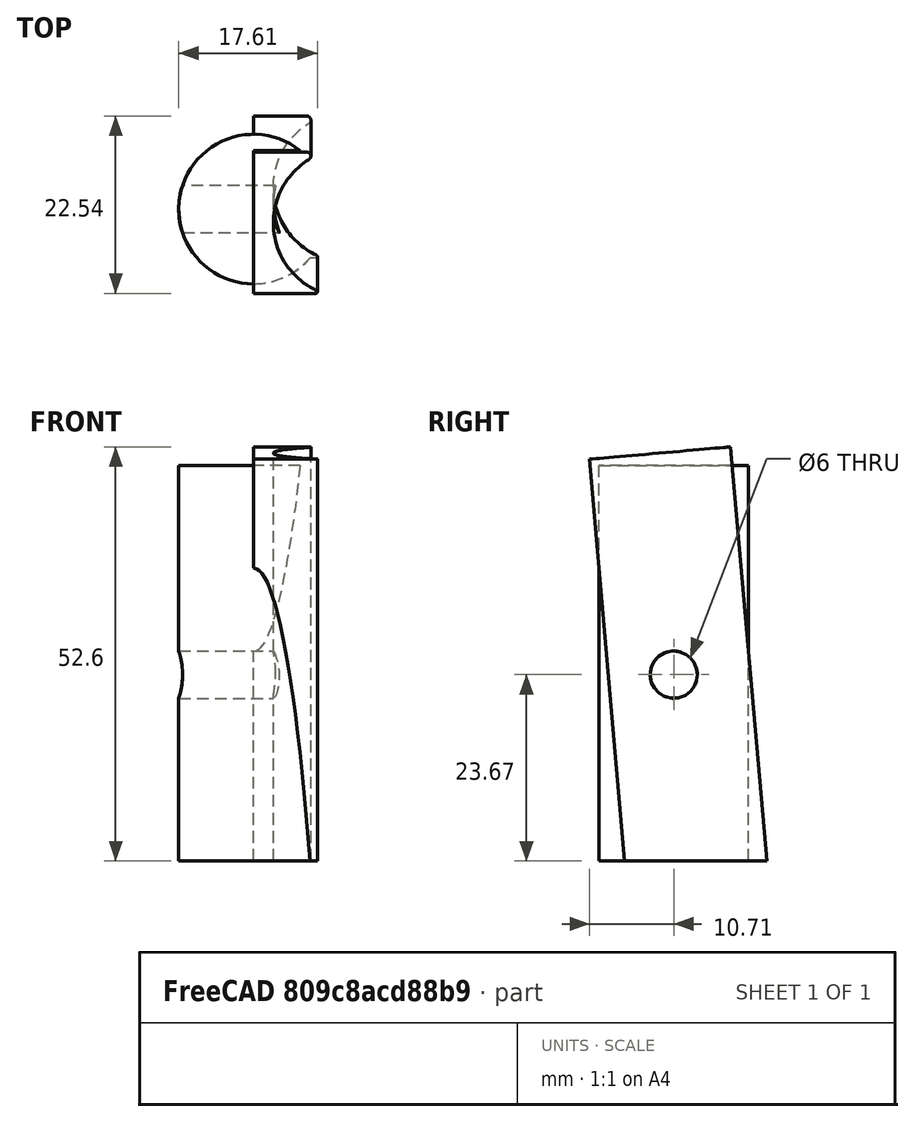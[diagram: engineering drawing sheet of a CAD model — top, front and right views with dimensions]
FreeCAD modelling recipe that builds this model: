
FCSTD DOCUMENT  (FreeCAD 0.19R)
Label: Mowerhandle.stl
License: All rights reserved
LicenseURL: http://en.wikipedia.org/wiki/All_rights_reserved
objects: Sketcher::SketchObject×3, PartDesign::Pocket×3, Mesh::Feature×2, PartDesign::Fillet×2, Part::Cylinder×1, Part::Box×1, Part::MultiFuse×1, PartDesign::FeatureBase×1, PartDesign::Body×1
note: 18 computed .brp shape members not serialized (recipe doc carries the construction recipe); baked Part::Feature solids carry a one-line shape summary decoded from their .brp

FEATURE [Mesh::Feature] MowerHandel
FEATURE [Part::Cylinder] Cylinder
  Angle = 360
  AttacherType = Attacher::AttachEngine3D
  Height = 53
  Radius = 9.5
FEATURE [Part::Box] Box  label="Cube"
  AttacherType = Attacher::AttachEngine3D
  Height = 54
  Length = 10
  Placement = pos=(0,-6,0) rot=(1,0,0;0.087266rad)
  Width = 18
FEATURE [Part::MultiFuse] Fusion
  Shapes = -> [Cylinder,Box]
FEATURE [PartDesign::FeatureBase] BaseFeature
  BaseFeature = -> Fusion
FEATURE [Sketcher::SketchObject] Sketch
  FullyConstrained = false
  MapMode = 5
  Placement = pos=(0,-4.75199,54.3155) rot=(1,0,0;0.087266rad)
  Support = -> [BaseFeature]
  sketch-geometry (1):
    g0: Circle CenterX=12.0222 CenterY=3.0075 CenterZ=0 NormalX=0 NormalY=0 NormalZ=1 AngleXU=0 Radius=9.5
  constraints (1):
    c: Radius(g0) = 9.5
FEATURE [PartDesign::Pocket] Pocket
  BaseFeature = -> BaseFeature
  Length = 5
  Length2 = 100
  Profile = -> Sketch
  Type = 1
FEATURE [PartDesign::Fillet] Fillet
  Base = -> Pocket [Edge13]
  BaseFeature = -> Pocket
  Radius = 0.5
  SupportTransform = false
FEATURE [PartDesign::Fillet] Fillet001
  Base = -> Fillet [Edge3]
  BaseFeature = -> Fillet
  Radius = 0.2
  SupportTransform = false
FEATURE [Sketcher::SketchObject] Sketch001
  FullyConstrained = false
  MapMode = 5
  Placement = pos=(0,0,0) rot=(0.57735,0.57735,0.57735;2.0944rad)
  Support = -> [YZ_Plane]
  sketch-geometry (1):
    g0: Circle CenterX=0 CenterY=26.4299 CenterZ=0 NormalX=0 NormalY=0 NormalZ=1 AngleXU=0 Radius=3
  constraints (2):
    c: PointOnObject(g0,g-2)
    c: Diameter(g0) = 6
FEATURE [PartDesign::Pocket] Pocket001
  BaseFeature = -> Fillet001
  Length = 5
  Length2 = 100
  Midplane = true
  Profile = -> Sketch001
  Type = 1
FEATURE [Sketcher::SketchObject] Sketch002
  FullyConstrained = false
  MapMode = 5
  Placement = pos=(0,0,0) rot=(0.57735,0.57735,0.57735;2.0944rad)
  Support = -> [YZ_Plane]
  sketch-geometry (4):
    g0: LineSegment StartX=-12.9286 StartY=2.76123 StartZ=0 EndX=17.649 EndY=2.76123 EndZ=0
    g1: LineSegment StartX=17.649 StartY=2.76123 StartZ=0 EndX=17.649 EndY=-9.03295 EndZ=0
    g2: LineSegment StartX=17.649 StartY=-9.03295 StartZ=0 EndX=-12.9286 EndY=-9.03295 EndZ=0
    g3: LineSegment StartX=-12.9286 StartY=-9.03295 StartZ=0 EndX=-12.9286 EndY=2.76123 EndZ=0
  constraints (8):
    c: Coincident(g0,g1)
    c: Coincident(g1,g2)
    c: Coincident(g2,g3)
    c: Coincident(g3,g0)
    c: Horizontal(g0)
    c: Horizontal(g2)
    c: Vertical(g1)
    c: Vertical(g3)
FEATURE [PartDesign::Pocket] Pocket002
  BaseFeature = -> Pocket001
  Length = 5
  Length2 = 100
  Midplane = true
  Profile = -> Sketch002
  Type = 1
FEATURE [PartDesign::Body] Body
  BaseFeature = -> Fusion
  Group = -> [BaseFeature,Sketch,Pocket,Fillet,Fillet001,Sketch001,Pocket001,Sketch002,Pocket002]
  Origin = -> Origin
  Tip = -> Pocket002
FEATURE [Mesh::Feature] Mesh  label="Pocket002 (Meshed)"
